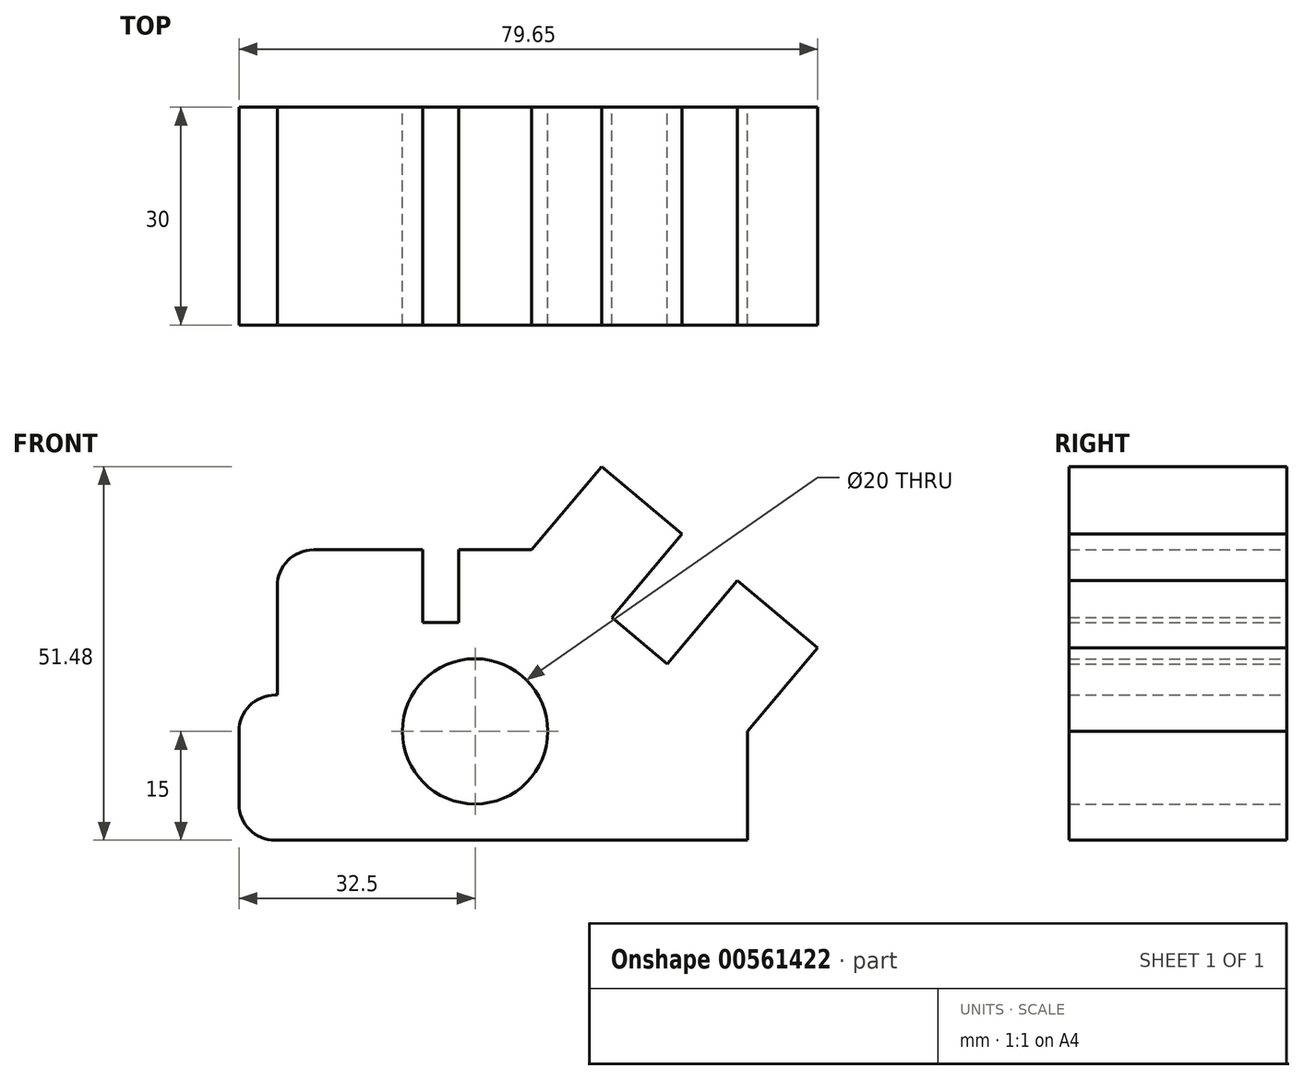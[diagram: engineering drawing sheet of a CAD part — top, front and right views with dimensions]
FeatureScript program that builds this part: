
annotation { "Feature Type Name" : "Feature", "Feature Type Description" : "" }
export const myFeature = defineFeature(function(context is Context, id is Id, definition is map)
    precondition{}
    {
        {
            var Q0;
            Q0=qCreatedBy(makeId("Front.planeOp"),FACE);
            var sketch = newSketch(context, id + "F0", { "sketchPlane" : qUnion([Q0])});
            skCircle(sketch, "E0", {"center": v(0, 0) * mm, "radius": 10 * mm});
            skLineSegment(sketch, "E1", {"start": v(-27.5, -15) * mm, "end": v(37.5, -15) * mm});
            skLineSegment(sketch, "E2", {"start": v(37.5, -15) * mm, "end": v(37.5, 0) * mm});
            skLineSegment(sketch, "E3", {"start": v(37.5, 0) * mm, "end": v(47.15, 11.48) * mm});
            skLineSegment(sketch, "E4", {"start": v(47.15, 11.48) * mm, "end": v(36.12, 20.76) * mm});
            skLineSegment(sketch, "E5", {"start": v(36.12, 20.76) * mm, "end": v(26.46, 9.28) * mm});
            skLineSegment(sketch, "E6", {"start": v(26.46, 9.28) * mm, "end": v(18.8, 15.72) * mm});
            skLineSegment(sketch, "E7", {"start": v(18.8, 15.72) * mm, "end": v(28.46, 27.2) * mm});
            skLineSegment(sketch, "E8", {"start": v(28.46, 27.2) * mm, "end": v(17.43, 36.48) * mm});
            skLineSegment(sketch, "E9", {"start": v(17.43, 36.48) * mm, "end": v(7.77, 25) * mm});
            skLineSegment(sketch, "E10", {"start": v(7.77, 25) * mm, "end": v(-2.23, 25) * mm});
            skLineSegment(sketch, "E11", {"start": v(-7.23, 25) * mm, "end": v(-22.23, 25) * mm});
            skLineSegment(sketch, "E12", {"start": v(-27.23, 20) * mm, "end": v(-27.23, 5) * mm});
            skLineSegment(sketch, "E13", {"start": v(-27.23, 5) * mm, "end": v(-27.5, 5) * mm});
            skLineSegment(sketch, "E14", {"start": v(-32.5, 0) * mm, "end": v(-32.5, -10) * mm});
            skLineSegment(sketch, "E15", {"start": v(-7.23, 25) * mm, "end": v(-7.23, 15) * mm});
            skLineSegment(sketch, "E16", {"start": v(-7.23, 15) * mm, "end": v(-2.23, 15) * mm});
            skLineSegment(sketch, "E17", {"start": v(-2.23, 15) * mm, "end": v(-2.23, 25) * mm});
            skPoint(sketch, "E18.visualSharp", {"position": v(-27.23, 25) * mm});
            skArc(sketch, "E18.filletArc", {"start": v(-22.23, 25) * mm, "mid": v(-25.76, 23.54) * mm, "end": v(-27.23, 20) * mm});
            skPoint(sketch, "E19.visualSharp", {"position": v(-32.5, 5) * mm});
            skArc(sketch, "E19.filletArc", {"start": v(-27.5, 5) * mm, "mid": v(-31.04, 3.54) * mm, "end": v(-32.5, 0) * mm});
            skPoint(sketch, "E20.visualSharp", {"position": v(-32.5, -15) * mm});
            skArc(sketch, "E20.filletArc", {"start": v(-32.5, -10) * mm, "mid": v(-31.04, -13.54) * mm, "end": v(-27.5, -15) * mm});
            skSolve(sketch);
        }
        {
            var Q0;
            Q0=qSketchRegion(id+"F0",true);
            extrude(context, id + "F1", {"entities" : qUnion([Q0]), "depth" : 30 * mm, "offsetDistance" : 25 * mm});
        }
    });
